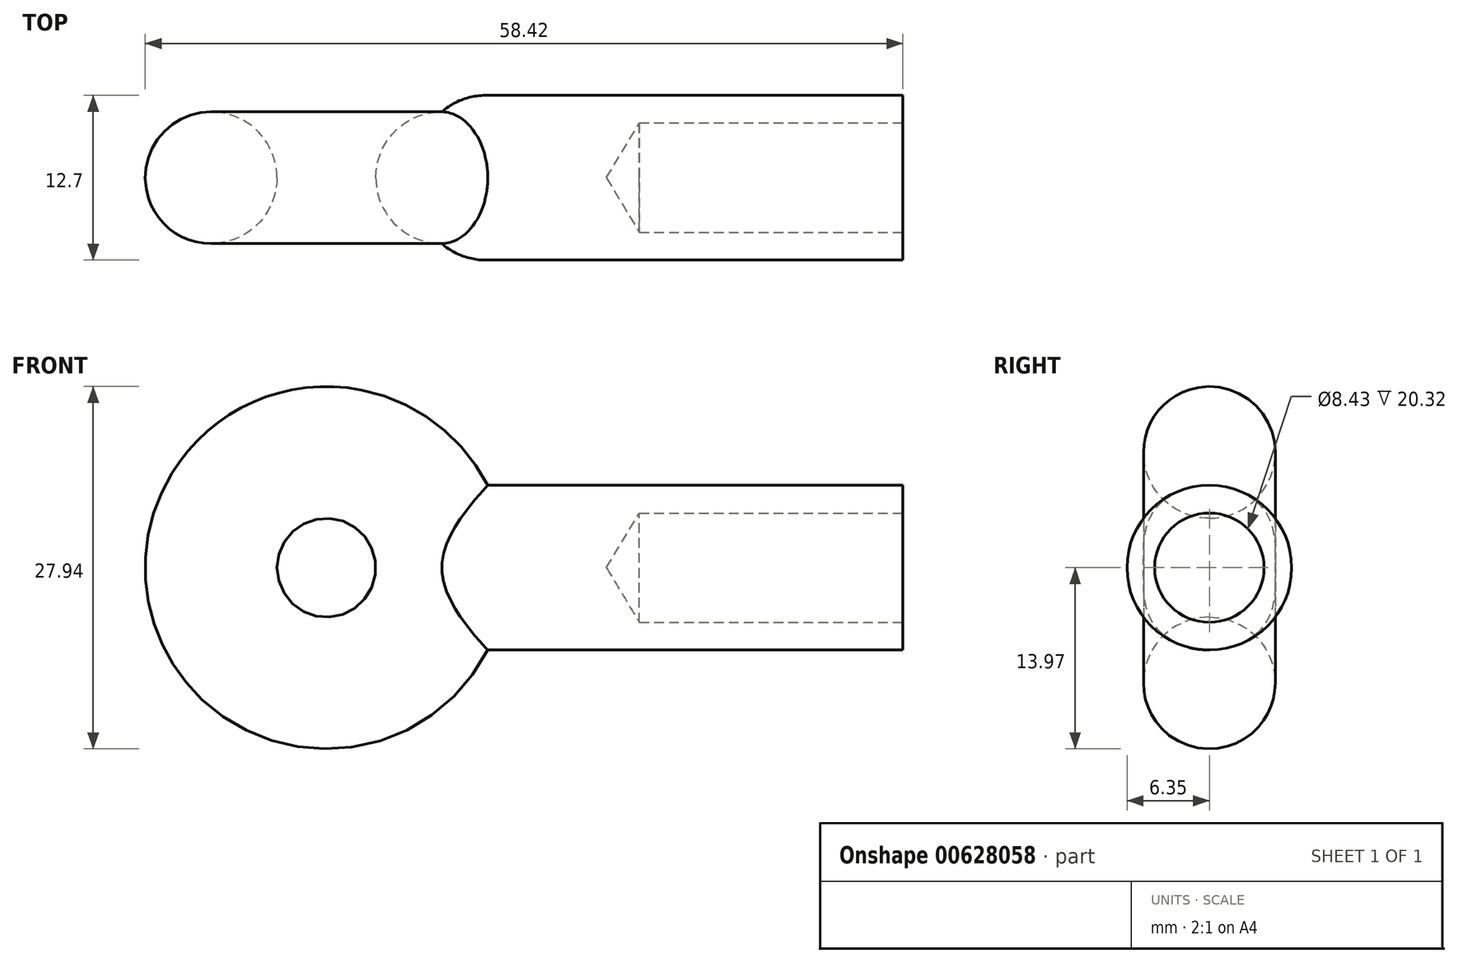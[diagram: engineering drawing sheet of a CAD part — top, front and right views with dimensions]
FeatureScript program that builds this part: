
annotation { "Feature Type Name" : "Feature", "Feature Type Description" : "" }
export const myFeature = defineFeature(function(context is Context, id is Id, definition is map)
    precondition{}
    {
        {
            var Q0;
            Q0=qCreatedBy(makeId("Right.planeOp"),FACE);
            var sketch = newSketch(context, id + "F0", { "sketchPlane" : qUnion([Q0])});
            skCircle(sketch, "E0", {"center": v(0, 8.9) * mm, "radius": 5.08 * mm});
            skLineSegment(sketch, "E1", {"start": v(-18.01, 0) * mm, "end": v(18.01, 0) * mm, "construction": true});
            skSolve(sketch);
        }
        {
            var Q0;
            Q0 = qSketchRegion(id + "F0", true);
            var Q1;
            Q1=sQuery(id+"F0.wireOp",EDGE,"E1");
            revolve(context, id + "F1", {"entities" : qUnion([Q0]), "axis" : qUnion([Q1]), "revolveType" : RevolveType.FULL});
        }
        {
            var Q0;
            Q0=qCreatedBy(makeId("Right.planeOp"),FACE);
            cPlane(context, id + "F2", {"entities" : qUnion([Q0]), "cplaneType" : CPlaneType.OFFSET, "offset" : 44.45 * mm, "width" : 152.4 * mm, "height" : 152.4 * mm});
        }
        {
            var Q0;
            Q0=qCreatedBy(id+"F2.planeOp",FACE);
            var sketch = newSketch(context, id + "F3", { "sketchPlane" : qUnion([Q0])});
            skCircle(sketch, "E2", {"center": v(0, 0) * mm, "radius": 6.35 * mm});
            skSolve(sketch);
        }
        {
            var Q0;
            Q0 = qSketchRegion(id + "F3", true);
            extrude(context, id + "F4", {"entities" : qUnion([Q0]), "oppositeDirection" : true, "depth" : 38.1 * mm, "offsetDistance" : 25.4 * mm});
        }
        {
            var Q0;
            Q0=makeQuery(id+"F4.opExtrude","CAP_EDGE",EDGE,{"disambiguationData":[OSD([sQuery(id+"F3.wireOp",EDGE,"E2")])],"isStart":false});
            chamfer(context, id + "F5", {"entities" : qUnion([Q0]), "width" : 3.8 * mm, "tangentPropagation" : true});
        }
        {
            var Q0;
            Q0=makeQuery(id+"F1.opRevolve","SWEPT_BODY",BODY,{"disambiguationData":[OSD([sQuery(id+"F0.wireOp",EDGE,"E0")])]});
            var Q1;
            Q1=makeQuery(id+"F4.opExtrude","SWEPT_BODY",BODY,{"disambiguationData":[OSD([sQuery(id+"F3.wireOp",EDGE,"E2")])]});
            booleanBodies(context, id + "F6", {"operationType" : BooleanOperationType.UNION, "tools" : qUnion([Q0, Q1])});
        }
        {
            var Q0;
            {var subQ0=sQuery(id+"F3.wireOp",EDGE,"E2");Q0=makeQuery(id+"F6.opBoolean","SPLIT",EDGE,{"disambiguationData":[OD(1.0)],"derivedFrom":makeQuery(id+"F5.opChamfer","BLEND_EDGE",EDGE,{"blendedFrom":[makeQuery(id+"F4.opExtrude","CAP_EDGE",EDGE,{"disambiguationData":[OSD([subQ0])],"isStart":false}),makeQuery(id+"F4.opExtrude","SWEPT_FACE",FACE,{"disambiguationData":[OSD([subQ0])]})],"blendedInto":[makeQuery(id+"F4.opExtrude","SWEPT_FACE",FACE,{"disambiguationData":[OSD([subQ0])]})]})});}
            var Q1;
            {var subQ0=sQuery(id+"F3.wireOp",EDGE,"E2");Q1=makeQuery(id+"F6.opBoolean","SPLIT",EDGE,{"disambiguationData":[OD(0.0)],"derivedFrom":makeQuery(id+"F5.opChamfer","BLEND_EDGE",EDGE,{"blendedFrom":[makeQuery(id+"F4.opExtrude","CAP_EDGE",EDGE,{"disambiguationData":[OSD([subQ0])],"isStart":false}),makeQuery(id+"F4.opExtrude","SWEPT_FACE",FACE,{"disambiguationData":[OSD([subQ0])]})],"blendedInto":[makeQuery(id+"F4.opExtrude","SWEPT_FACE",FACE,{"disambiguationData":[OSD([subQ0])]})]})});}
            fillet(context, id + "F7", {"entities" : qUnion([Q0, Q1]), "radius" : 5.08 * mm, "tangentPropagation" : true, "allowEdgeOverflow" : false});
        }
        {
            var Q0;
            Q0=makeQuery(id+"F4.opExtrude","CAP_FACE",FACE,{"disambiguationData":[OSD([sQuery(id+"F3.wireOp",EDGE,"E2")])],"isStart":true});
            var sketch = newSketch(context, id + "F8", { "sketchPlane" : qUnion([Q0])});
            skPoint(sketch, "E3", {"position": v(0, 0) * mm});
            skSolve(sketch);
        }
        {
            var Q0;
            Q0=sQuery(id+"F8.wireOp",VERTEX,"E3");
            var Q1;
            Q1=makeQuery(id+"F1.opRevolve","SWEPT_BODY",BODY,{"disambiguationData":[OSD([sQuery(id+"F0.wireOp",EDGE,"E0")])]});
            hole(context, id + "F9", {"style" : HoleStyle.SIMPLE, "endStyle" : HoleEndStyle.BLIND, "standardTappedOrClearance" : lookupTablePath({ "standard" : "ANSI", "engagement" : "75%", "pitch" : "24 tpi", "size" : "3/8", "type" : "Tapped" }), "standardBlindInLast" : lookupTablePath({ "standard" : "ANSI", "engagement" : "75%", "pitch" : "24 tpi", "size" : "3/8", "type" : "Tapped" }), "holeDiameter" : 8.43 * mm, "majorDiameter" : 9.52 * mm, "showTappedDepth" : true, "holeDepth" : 20.32 * mm, "isTappedThrough" : true, "tappedDepth" : 17.14 * mm, "tapClearance" : 3, "startFromSketch" : true, "locations" : qUnion([Q0]), "scope" : qUnion([Q1])});
        }
    });
